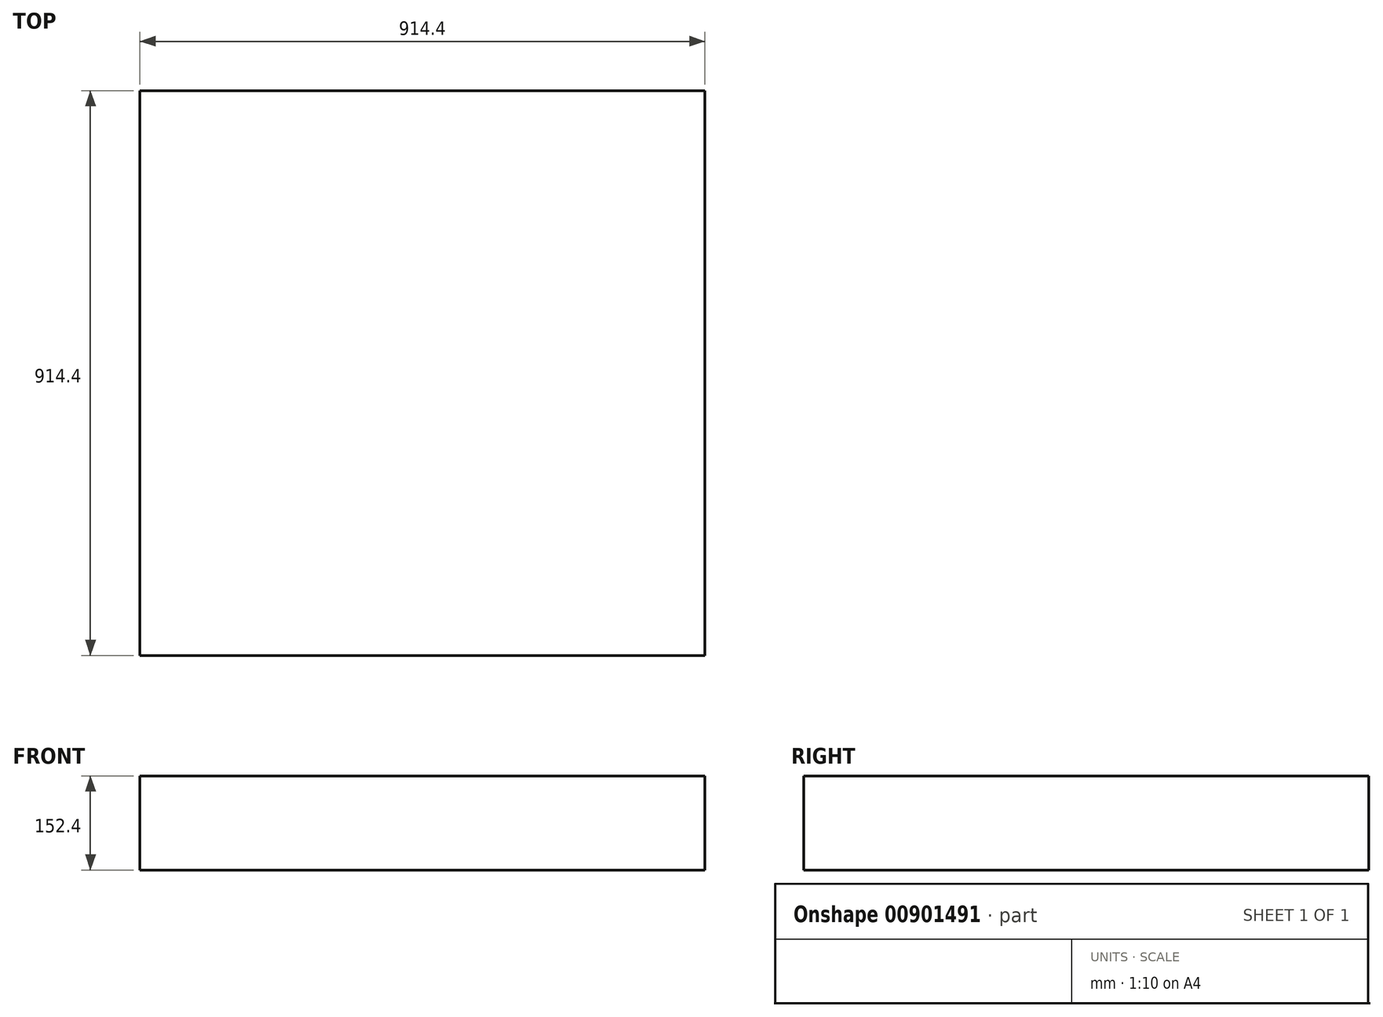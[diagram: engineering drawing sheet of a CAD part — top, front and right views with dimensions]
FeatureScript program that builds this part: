
annotation { "Feature Type Name" : "Feature", "Feature Type Description" : "" }
export const myFeature = defineFeature(function(context is Context, id is Id, definition is map)
    precondition{}
    {
        {
            var Q0;
            Q0=qCreatedBy(makeId("Top.planeOp"),FACE);
            var sketch = newSketch(context, id + "F0", { "sketchPlane" : qUnion([Q0])});
            skLineSegment(sketch, "E0.bottom", {"start": v(457.2, -457.2) * mm, "end": v(-457.2, -457.2) * mm});
            skLineSegment(sketch, "E0.top", {"start": v(457.2, 457.2) * mm, "end": v(-457.2, 457.2) * mm});
            skLineSegment(sketch, "E0.left", {"start": v(457.2, -457.2) * mm, "end": v(457.2, 457.2) * mm});
            skLineSegment(sketch, "E0.right", {"start": v(-457.2, -457.2) * mm, "end": v(-457.2, 457.2) * mm});
            skPoint(sketch, "E0.middle", {"position": v(0, 0) * mm});
            skSolve(sketch);
        }
        {
            var Q0;
            Q0 = qSketchRegion(id + "F0", true);
            extrude(context, id + "F1", {"entities" : qUnion([Q0]), "endBound" : BoundingType.SYMMETRIC, "depth" : 152.4 * mm, "offsetDistance" : 25.4 * mm});
        }
    });
